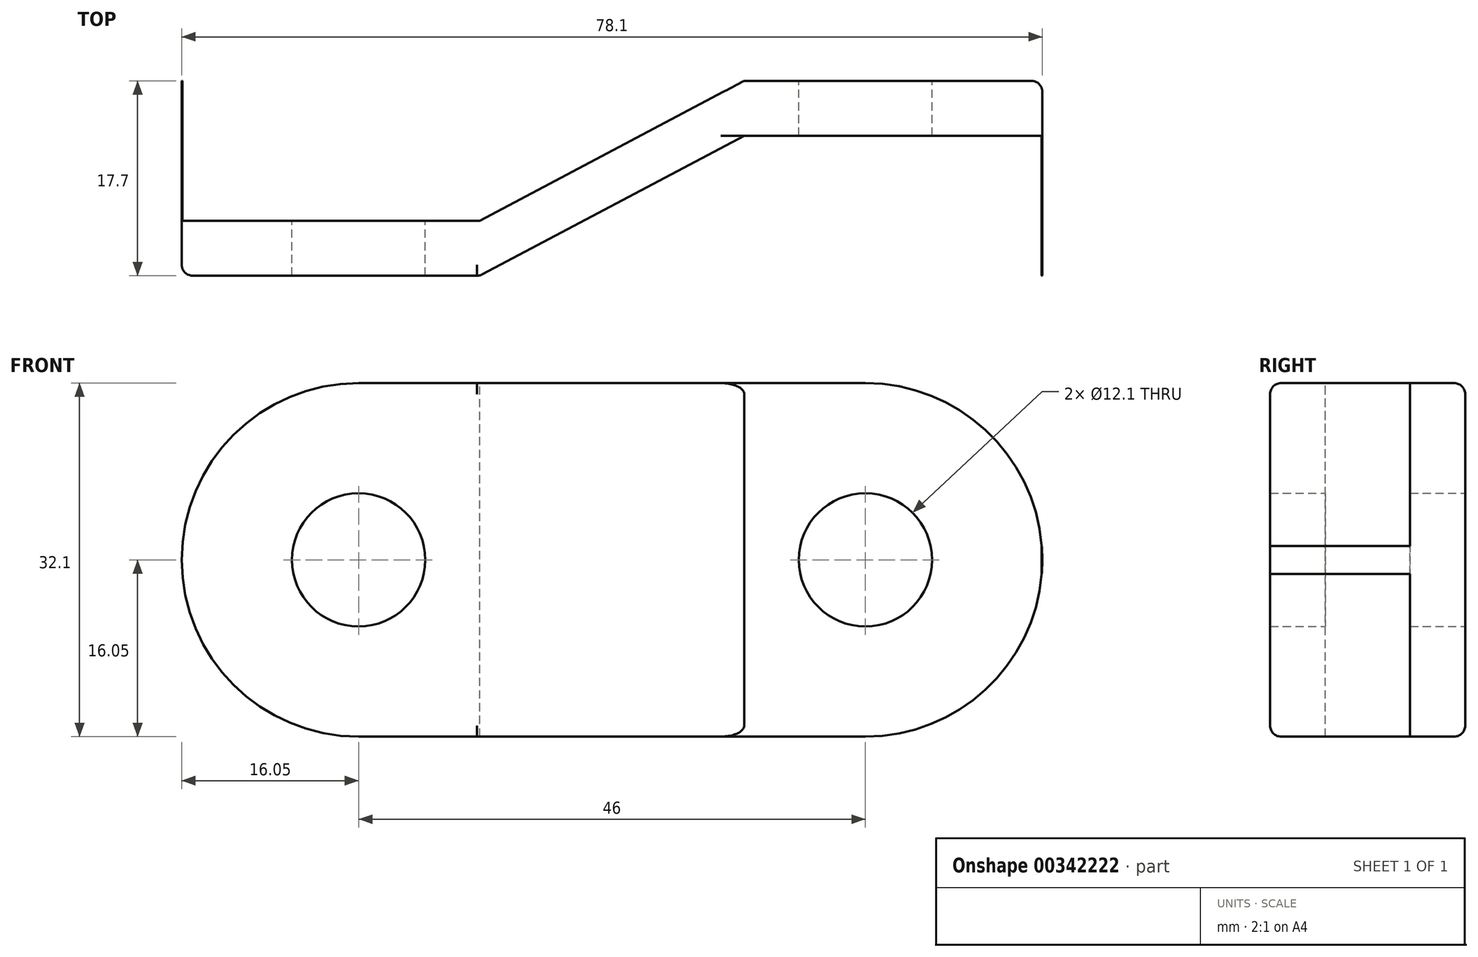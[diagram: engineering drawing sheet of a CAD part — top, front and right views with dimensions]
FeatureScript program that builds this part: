
annotation { "Feature Type Name" : "Feature", "Feature Type Description" : "" }
export const myFeature = defineFeature(function(context is Context, id is Id, definition is map)
    precondition{}
    {
        {
            var Q0;
            Q0=qCreatedBy(makeId("Front.planeOp"),FACE);
            var sketch = newSketch(context, id + "F0", { "sketchPlane" : qUnion([Q0])});
            skCircle(sketch, "E0", {"center": v(-46, 6.05) * mm, "radius": 6.05 * mm});
            skCircle(sketch, "E1", {"center": v(0, 6.05) * mm, "radius": 6.05 * mm});
            skArc(sketch, "E2.0", {"start": v(-46, 22.1) * mm, "mid": v(-62.05, 6.05) * mm, "end": v(-46, -10) * mm});
            skArc(sketch, "E3.0", {"start": v(0, -10) * mm, "mid": v(16.05, 6.05) * mm, "end": v(0, 22.1) * mm});
            skLineSegment(sketch, "E4", {"start": v(0, -10) * mm, "end": v(-46, -10) * mm});
            skLineSegment(sketch, "E5", {"start": v(-46, 22.1) * mm, "end": v(0, 22.1) * mm});
            skPoint(sketch, "E6.bottom.end.orphan", {"position": v(-46, 0) * mm});
            skPoint(sketch, "E6.bottom.start.orphan", {"position": v(0, 0) * mm});
            skPoint(sketch, "E7.trimOffspring.end.orphan", {"position": v(-46, 12.1) * mm});
            skPoint(sketch, "E6.top.start.orphan", {"position": v(0, 12.1) * mm});
            skSolve(sketch);
        }
        {
            var Q0;
            Q0=qCreatedBy(makeId("Top.planeOp"),FACE);
            var sketch = newSketch(context, id + "F1", { "sketchPlane" : qUnion([Q0])});
            skLineSegment(sketch, "E8.bottom", {"start": v(0, 0) * mm, "end": v(-46, 0) * mm});
            skLineSegment(sketch, "E8.top", {"start": v(0, -17.7) * mm, "end": v(-46, -17.7) * mm});
            skLineSegment(sketch, "E9.bottom", {"start": v(-46, 0) * mm, "end": v(-62, 0) * mm});
            skLineSegment(sketch, "E9.top", {"start": v(-46, -17.7) * mm, "end": v(-62, -17.7) * mm});
            skLineSegment(sketch, "E9.right", {"start": v(-62, 0) * mm, "end": v(-62, -17.7) * mm});
            skLineSegment(sketch, "E10.bottom", {"start": v(0, 0) * mm, "end": v(16, 0) * mm});
            skLineSegment(sketch, "E10.top", {"start": v(0, -17.7) * mm, "end": v(16, -17.7) * mm});
            skLineSegment(sketch, "E10.right", {"start": v(16, 0) * mm, "end": v(16, -17.7) * mm});
            skLineSegment(sketch, "E11", {"start": v(-46, -12.7) * mm, "end": v(-40, -12.7) * mm});
            skLineSegment(sketch, "E12", {"start": v(0, -5) * mm, "end": v(-6, -5) * mm});
            skLineSegment(sketch, "E13", {"start": v(0, -5) * mm, "end": v(16, -5) * mm});
            skLineSegment(sketch, "E14", {"start": v(16, -5) * mm, "end": v(16, 0) * mm});
            skLineSegment(sketch, "E15", {"start": v(-46, -12.7) * mm, "end": v(-62, -12.7) * mm});
            skLineSegment(sketch, "E16", {"start": v(-40, -12.7) * mm, "end": v(-35, -12.7) * mm});
            skLineSegment(sketch, "E17", {"start": v(-6, 0) * mm, "end": v(-11, 0) * mm});
            skLineSegment(sketch, "E18", {"start": v(-6, -5) * mm, "end": v(-11, -5) * mm});
            skLineSegment(sketch, "E19", {"start": v(-40, -17.7) * mm, "end": v(-35, -17.7) * mm});
            skLineSegment(sketch, "E20", {"start": v(-11, 0) * mm, "end": v(-35, -12.7) * mm});
            skLineSegment(sketch, "E21", {"start": v(-35, -17.7) * mm, "end": v(-11, -5) * mm});
            skSolve(sketch);
        }
        {
            var Q0;
            Q0=makeQuery(id+"F0.imprint","IMPRINT",FACE,{"disambiguationData":[TD([[makeQuery(id+"F0.imprint","IMPRINT",EDGE,{"derivedFrom":sQuery(id+"F0.wireOp",EDGE,"E0")}),-1.0]])]});
            extrude(context, id + "F2", {"entities" : qUnion([Q0]), "depth" : 17.7 * mm});
        }
        {
            var Q0;
            {var subQ1=sQuery(id+"F1.wireOp",EDGE,"E9.bottom");Q0=makeQuery(id+"F1.imprint","IMPRINT",FACE,{"disambiguationData":[TD([[makeQuery(id+"F1.imprint","IMPRINT",EDGE,{"derivedFrom":subQ1}),1.0]])]});}
            var Q1;
            {var subQ0=sQuery(id+"F1.wireOp",EDGE,"E10.top");Q1=makeQuery(id+"F1.imprint","IMPRINT",FACE,{"disambiguationData":[TD([[makeQuery(id+"F1.imprint","IMPRINT",EDGE,{"derivedFrom":subQ0}),1.0]])]});}
            extrude(context, id + "F3", {"entities" : qUnion([Q0, Q1]), "operationType" : NewBodyOperationType.REMOVE, "endBound" : BoundingType.THROUGH_ALL, "oppositeDirection" : true, "depth" : 25.4 * mm, "hasSecondDirection" : true, "secondDirectionBound" : SecondDirectionBoundingType.THROUGH_ALL, "secondDirectionOppositeDirection" : false, "secondDirectionDepth" : 25.4 * mm});
        }
        {
            var Q0;
            Q0=makeQuery(id+"F3.boolean.opBoolean","INTERSECT",EDGE,{"derivedFrom":[makeQuery(id+"F2.opExtrude","SWEPT_FACE",FACE,{"disambiguationData":[OSD([sQuery(id+"F0.wireOp",EDGE,"E4")])]}),makeQuery(id+"F3.opExtrude","SWEPT_FACE",FACE,{"disambiguationData":[OSD([sQuery(id+"FQSPgtal8AffcxS_1.wireOp",EDGE,"z9Lnjqcm-uTf0-5htj-WNHY-aYB5GANBnTNq")])]})]});
            var Q1;
            Q1=makeQuery(id+"F2.opExtrude","CAP_EDGE",EDGE,{"disambiguationData":[OSD([sQuery(id+"F0.wireOp",EDGE,"E2.0")])],"isStart":false});
            var Q2;
            Q2=makeQuery(id+"F3.boolean.opBoolean","INTERSECT",EDGE,{"derivedFrom":[makeQuery(id+"F2.opExtrude","SWEPT_FACE",FACE,{"disambiguationData":[OSD([sQuery(id+"F0.wireOp",EDGE,"E5")])]}),makeQuery(id+"F3.opExtrude","SWEPT_FACE",FACE,{"disambiguationData":[OSD([sQuery(id+"FQSPgtal8AffcxS_1.wireOp",EDGE,"z9Lnjqcm-uTf0-5htj-WNHY-aYB5GANBnTNq")])]})]});
            var Q3;
            Q3=makeQuery(id+"F3.boolean.opBoolean","INTERSECT",EDGE,{"derivedFrom":[makeQuery(id+"F2.opExtrude","SWEPT_FACE",FACE,{"disambiguationData":[OSD([sQuery(id+"F0.wireOp",EDGE,"E3.0")])]}),makeQuery(id+"F3.opExtrude","SWEPT_FACE",FACE,{"disambiguationData":[OSD([sQuery(id+"FQSPgtal8AffcxS_1.wireOp",EDGE,"D9kL7Tnl-Cn1T-XNyD-1og5-mdiD3M6EzMdl")])]})]});
            var Q4;
            Q4=makeQuery(id+"F3.boolean.opBoolean","INTERSECT",EDGE,{"derivedFrom":[makeQuery(id+"F2.opExtrude","SWEPT_FACE",FACE,{"disambiguationData":[OSD([sQuery(id+"F0.wireOp",EDGE,"E4")])]}),makeQuery(id+"F3.opExtrude","SWEPT_FACE",FACE,{"disambiguationData":[OSD([sQuery(id+"FQSPgtal8AffcxS_1.wireOp",EDGE,"zEOluQMj-HBuU-TlPN-pqLC-feIYMuG1uBPj")])]})]});
            var Q5;
            Q5=makeQuery(id+"F2.opExtrude","CAP_EDGE",EDGE,{"disambiguationData":[OSD([sQuery(id+"F0.wireOp",EDGE,"E3.0")])],"isStart":true});
            var Q6;
            Q6=makeQuery(id+"F3.boolean.opBoolean","INTERSECT",EDGE,{"derivedFrom":[makeQuery(id+"F2.opExtrude","SWEPT_FACE",FACE,{"disambiguationData":[OSD([sQuery(id+"F0.wireOp",EDGE,"E5")])]}),makeQuery(id+"F3.opExtrude","SWEPT_FACE",FACE,{"disambiguationData":[OSD([sQuery(id+"FQSPgtal8AffcxS_1.wireOp",EDGE,"zEOluQMj-HBuU-TlPN-pqLC-feIYMuG1uBPj")])]})]});
            var Q7;
            Q7=makeQuery(id+"F3.boolean.opBoolean","INTERSECT",EDGE,{"derivedFrom":[makeQuery(id+"F2.opExtrude","SWEPT_FACE",FACE,{"disambiguationData":[OSD([sQuery(id+"F0.wireOp",EDGE,"E2.0")])]}),makeQuery(id+"F3.opExtrude","SWEPT_FACE",FACE,{"disambiguationData":[OSD([sQuery(id+"FQSPgtal8AffcxS_1.wireOp",EDGE,"MdI8YLBJ-syx8-SRqm-nc8T-3YXMZ2Dzdl6J")])]})]});
            fillet(context, id + "F4", {"entities" : qUnion([Q0, Q1, Q2, Q3, Q4, Q5, Q6, Q7]), "radius" : 1 * mm, "tangentPropagation" : true, "allowEdgeOverflow" : false});
        }
        {
            var Q0;
            {var subQ1=sQuery(id+"F0.wireOp",EDGE,"E4");var subQ2=sQuery(id+"F1.wireOp",EDGE,"9lEzZxRY-OPI4-HqS6-A2ZP-Qpw240RFtuP4");Q0=makeQuery(id+"F3.boolean.opBoolean","COPY",EDGE,{"disambiguationData":[TD([makeQuery(id+"F2.opExtrude","SWEPT_FACE",FACE,{"disambiguationData":[OSD([subQ1])]})])],"derivedFrom":makeQuery(id+"F3.opExtrude","SWEPT_EDGE",EDGE,{"disambiguationData":[OSD([sQuery(id+"F1.wireOp",EDGE,"E8.top"),subQ2])]})});}
            var Q1;
            {var subQ0=sQuery(id+"F0.wireOp",EDGE,"E5");var subQ2=sQuery(id+"F1.wireOp",EDGE,"KDW0Modw-7wEz-YPRe-YzhD-Gml5BIk3j5gN");Q1=makeQuery(id+"F3.boolean.opBoolean","COPY",EDGE,{"disambiguationData":[TD([makeQuery(id+"F2.opExtrude","SWEPT_FACE",FACE,{"disambiguationData":[OSD([subQ0])]})])],"derivedFrom":makeQuery(id+"F3.opExtrude","SWEPT_EDGE",EDGE,{"disambiguationData":[OSD([sQuery(id+"F1.wireOp",EDGE,"E8.bottom"),subQ2])]})});}
            var Q2;
            {var subQ0=sQuery(id+"F0.wireOp",EDGE,"E4");var subQ2=sQuery(id+"F1.wireOp",EDGE,"KDW0Modw-7wEz-YPRe-YzhD-Gml5BIk3j5gN");Q2=makeQuery(id+"F3.boolean.opBoolean","COPY",EDGE,{"disambiguationData":[TD([makeQuery(id+"F2.opExtrude","SWEPT_FACE",FACE,{"disambiguationData":[OSD([subQ0])]})])],"derivedFrom":makeQuery(id+"F3.opExtrude","SWEPT_EDGE",EDGE,{"disambiguationData":[OSD([sQuery(id+"F1.wireOp",EDGE,"E8.bottom"),subQ2])]})});}
            var Q3;
            {var subQ1=sQuery(id+"F0.wireOp",EDGE,"E5");var subQ2=sQuery(id+"F1.wireOp",EDGE,"9lEzZxRY-OPI4-HqS6-A2ZP-Qpw240RFtuP4");Q3=makeQuery(id+"F3.boolean.opBoolean","COPY",EDGE,{"disambiguationData":[TD([makeQuery(id+"F2.opExtrude","SWEPT_FACE",FACE,{"disambiguationData":[OSD([subQ1])]})])],"derivedFrom":makeQuery(id+"F3.opExtrude","SWEPT_EDGE",EDGE,{"disambiguationData":[OSD([sQuery(id+"F1.wireOp",EDGE,"E8.top"),subQ2])]})});}
            fillet(context, id + "F5", {"entities" : qUnion([Q0, Q1, Q2, Q3]), "radius" : 1 * mm, "tangentPropagation" : true, "allowEdgeOverflow" : false});
        }
    });
